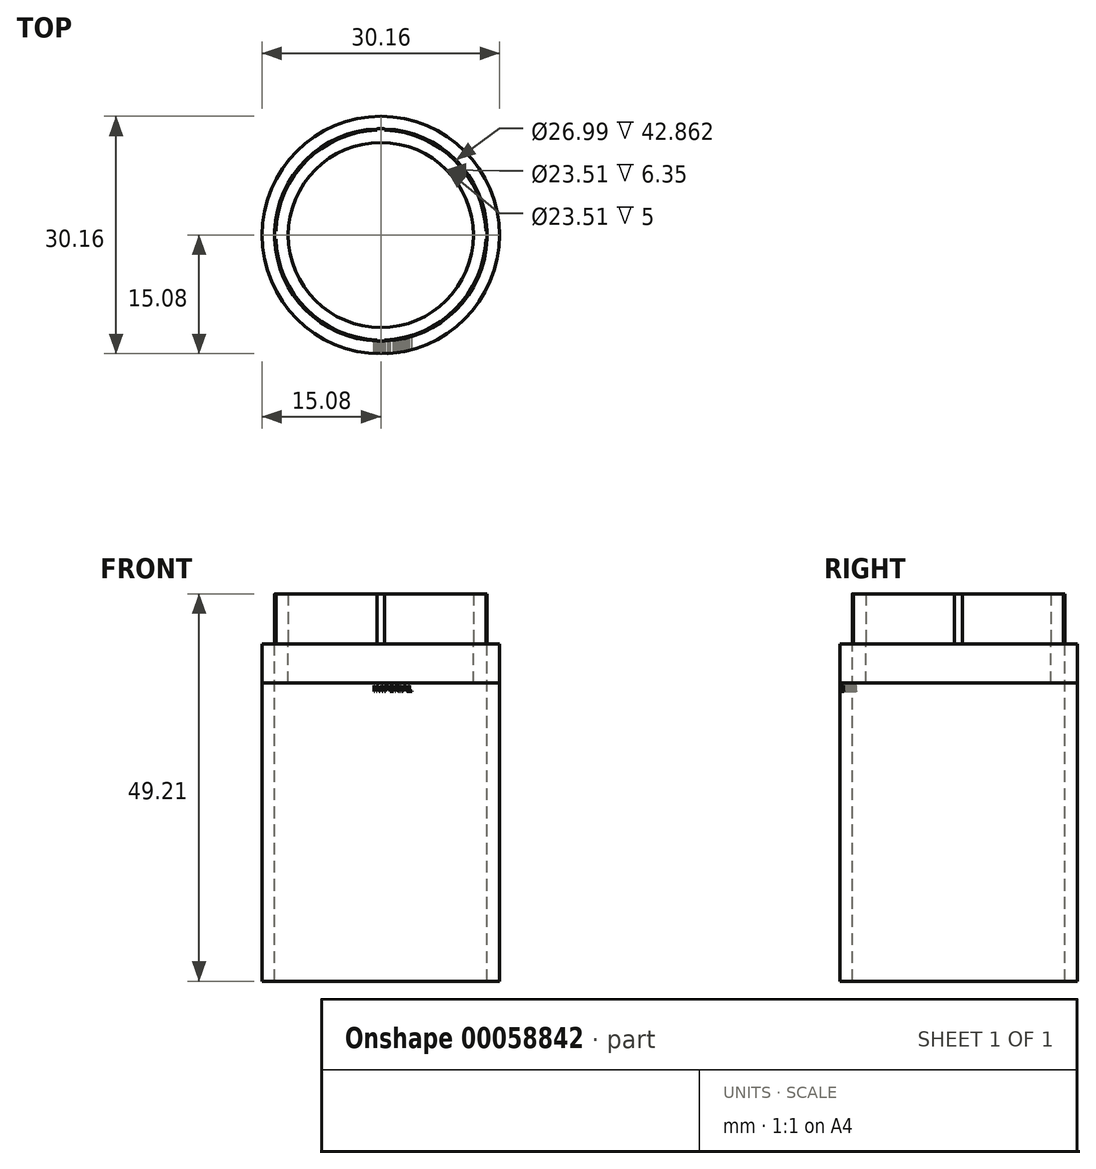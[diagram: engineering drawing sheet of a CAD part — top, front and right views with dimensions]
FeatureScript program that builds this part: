
annotation { "Feature Type Name" : "Feature", "Feature Type Description" : "" }
export const myFeature = defineFeature(function(context is Context, id is Id, definition is map)
    precondition{}
    {
        {
            var Q0;
            Q0=qCreatedBy(makeId("Top.planeOp"),FACE);
            var sketch = newSketch(context, id + "F0", { "sketchPlane" : qUnion([Q0])});
            skCircle(sketch, "E0", {"center": v(0, 0) * mm, "radius": 11.75 * mm});
            skCircle(sketch, "E1", {"center": v(0, 0) * mm, "radius": 13.34 * mm});
            skArc(sketch, "E2", {"start": v(13.48, -0.5) * mm, "mid": v(13.5, 0) * mm, "end": v(13.48, 0.5) * mm});
            skLineSegment(sketch, "E3", {"start": v(13.48, -0.5) * mm, "end": v(13.48, 0) * mm, "construction": true});
            skLineSegment(sketch, "E4", {"start": v(13.48, 0.5) * mm, "end": v(13.48, 0) * mm, "construction": true});
            skLineSegment(sketch, "E5", {"start": v(13.48, 0.5) * mm, "end": v(13.33, 0.5) * mm});
            skLineSegment(sketch, "E6", {"start": v(13.48, -0.5) * mm, "end": v(13.33, -0.5) * mm});
            skArc(sketch, "E7", {"start": v(0.5, 13.48) * mm, "mid": v(0, 13.5) * mm, "end": v(-0.5, 13.48) * mm});
            skLineSegment(sketch, "E8", {"start": v(-0.5, 13.48) * mm, "end": v(0, 13.48) * mm, "construction": true});
            skLineSegment(sketch, "E9", {"start": v(0.5, 13.48) * mm, "end": v(0, 13.48) * mm, "construction": true});
            skLineSegment(sketch, "E10", {"start": v(13.33, 0.5) * mm, "end": v(13.33, 0) * mm, "construction": true});
            skLineSegment(sketch, "E11", {"start": v(0.5, 13.48) * mm, "end": v(0.5, 13.33) * mm});
            skLineSegment(sketch, "E12", {"start": v(-0.5, 13.48) * mm, "end": v(-0.5, 13.33) * mm});
            skArc(sketch, "E13", {"start": v(-13.48, 0.5) * mm, "mid": v(-13.5, 0) * mm, "end": v(-13.48, -0.5) * mm});
            skLineSegment(sketch, "E14", {"start": v(-13.48, 0.5) * mm, "end": v(-13.48, 0) * mm, "construction": true});
            skLineSegment(sketch, "E15", {"start": v(-13.48, 0) * mm, "end": v(-13.48, -0.5) * mm, "construction": true});
            skLineSegment(sketch, "E16", {"start": v(-13.48, 0.5) * mm, "end": v(-13.33, 0.5) * mm});
            skLineSegment(sketch, "E17", {"start": v(-13.48, -0.5) * mm, "end": v(-13.33, -0.5) * mm});
            skArc(sketch, "E18", {"start": v(-0.5, -13.48) * mm, "mid": v(0, -13.5) * mm, "end": v(0.5, -13.48) * mm});
            skLineSegment(sketch, "E19", {"start": v(0.5, -13.48) * mm, "end": v(0, -13.48) * mm, "construction": true});
            skLineSegment(sketch, "E20", {"start": v(0, -13.48) * mm, "end": v(-0.5, -13.48) * mm, "construction": true});
            skLineSegment(sketch, "E21", {"start": v(0.5, -13.48) * mm, "end": v(0.5, -13.33) * mm});
            skLineSegment(sketch, "E22", {"start": v(-0.5, -13.48) * mm, "end": v(-0.5, -13.33) * mm});
            skSolve(sketch);
        }
        {
            var Q0;
            Q0=qSketchRegion(id+"F0",true);
            extrude(context, id + "F1", {"entities" : qUnion([Q0]), "depth" : 6.35 * mm});
        }
        {
            var Q0;
            Q0=qCreatedBy(makeId("Top.planeOp"),FACE);
            var sketch = newSketch(context, id + "F2", { "sketchPlane" : qUnion([Q0])});
            skCircle(sketch, "E23", {"center": v(0, 0) * mm, "radius": 13.5 * mm});
            skCircle(sketch, "E24", {"center": v(0, 0) * mm, "radius": 15.08 * mm});
            skSolve(sketch);
        }
        {
            var Q0;
            Q0=qSketchRegion(id+"F2",true);
            extrude(context, id + "F3", {"entities" : qUnion([Q0]), "operationType" : NewBodyOperationType.ADD, "oppositeDirection" : true, "depth" : 42.86 * mm});
        }
        {
            var Q0;
            Q0=qCreatedBy(makeId("Top.planeOp"),FACE);
            var sketch = newSketch(context, id + "F4", { "sketchPlane" : qUnion([Q0])});
            skCircle(sketch, "E25", {"center": v(0, 0) * mm, "radius": 11.75 * mm});
            skCircle(sketch, "E26", {"center": v(0, 0) * mm, "radius": 15.08 * mm});
            skSolve(sketch);
        }
        {
            var Q0;
            Q0 = qSketchRegion(id + "F4", true);
            extrude(context, id + "F5", {"entities" : qUnion([Q0]), "oppositeDirection" : true, "depth" : 5 * mm});
        }
        {
            var Q0;
            Q0=qCreatedBy(makeId("Front.planeOp"),FACE);
            var sketch = newSketch(context, id + "F6", { "sketchPlane" : qUnion([Q0])});
            skText(sketch, "E27", { "text": "IMPERIAL", "fontName": "OpenSans-Regular.ttf"});
            const initialGuessF6  = {"E27": [-0.00098, -0.00608, 1, 0, 0.00082]};
            skSetInitialGuess(sketch, initialGuessF6);
            skSolve(sketch);
        }
        {
            var Q0;
            Q0 = qSketchRegion(id + "F6", true);
            extrude(context, id + "F7", {"entities" : qUnion([Q0]), "operationType" : NewBodyOperationType.REMOVE, "depth" : 127 * mm});
        }
    });
